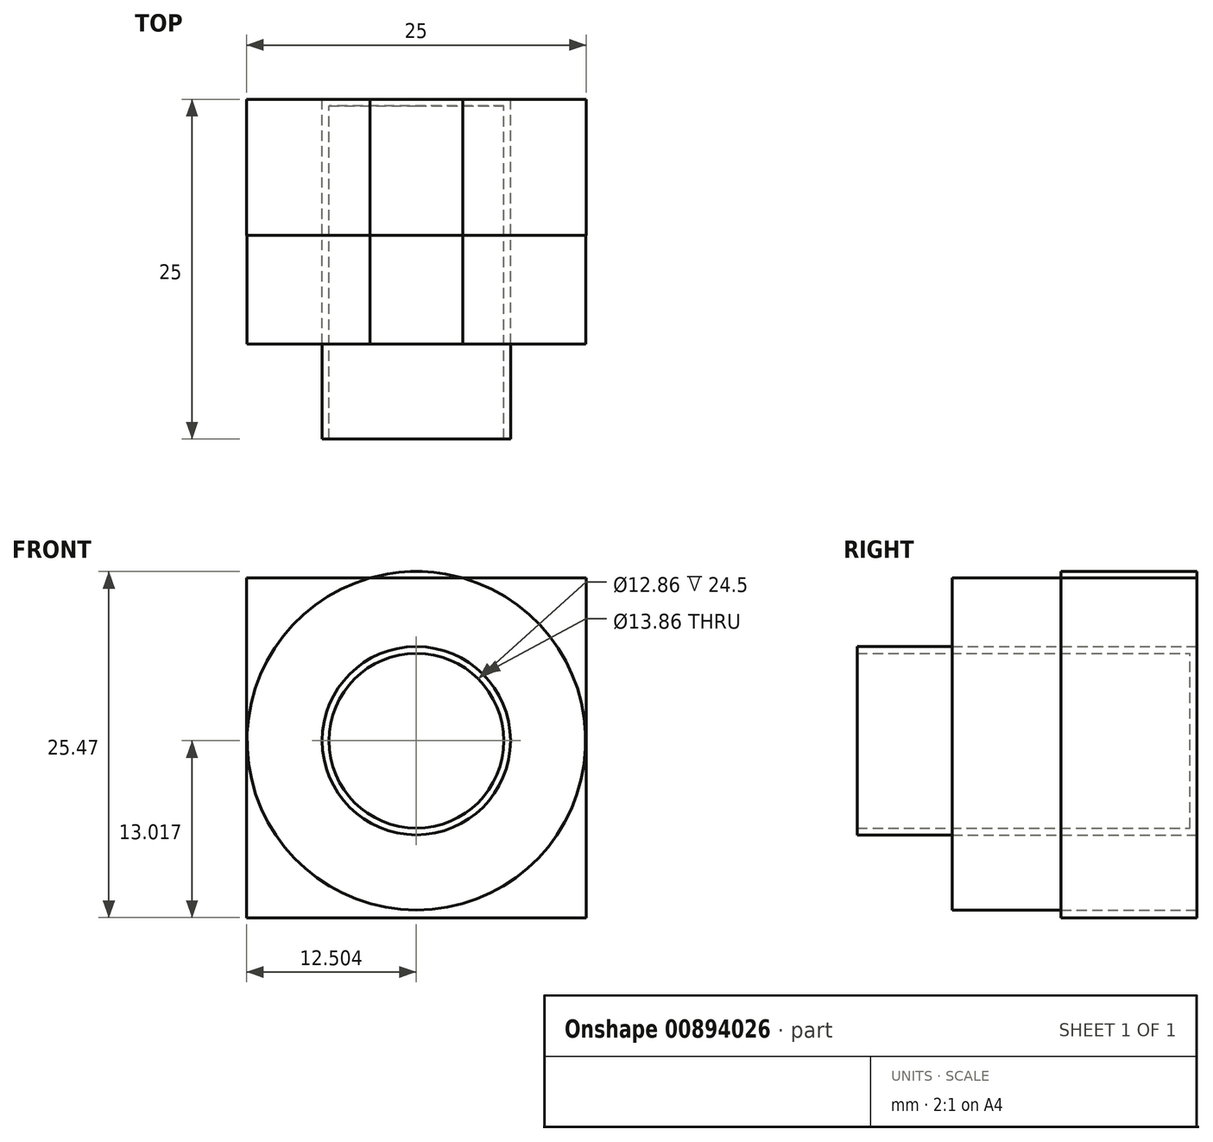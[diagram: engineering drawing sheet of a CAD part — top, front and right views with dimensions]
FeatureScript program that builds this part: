
annotation { "Feature Type Name" : "Feature", "Feature Type Description" : "" }
export const myFeature = defineFeature(function(context is Context, id is Id, definition is map)
    precondition{}
    {
        {
            var Q0;
            Q0=qCreatedBy(makeId("Front.planeOp"),FACE);
            var sketch = newSketch(context, id + "F0", { "sketchPlane" : qUnion([Q0])});
            skLineSegment(sketch, "E0.bottom", {"start": v(-12.07, -0.95) * mm, "end": v(-37.07, -0.95) * mm});
            skLineSegment(sketch, "E0.top", {"start": v(-12.07, 24.05) * mm, "end": v(-37.07, 24.05) * mm});
            skLineSegment(sketch, "E0.left", {"start": v(-12.07, -0.95) * mm, "end": v(-12.07, 24.05) * mm});
            skLineSegment(sketch, "E0.right", {"start": v(-37.07, -0.95) * mm, "end": v(-37.07, 24.05) * mm});
            skCircle(sketch, "E1", {"center": v(-24.57, 12.07) * mm, "radius": 12.45 * mm});
            skCircle(sketch, "E2", {"center": v(-24.57, 12.07) * mm, "radius": 6.93 * mm});
            skSolve(sketch);
        }
        {
            var Q0;
            Q0=makeQuery(id+"F0.imprint","IMPRINT",FACE,{"disambiguationData":[TD([[makeQuery(id+"F0.imprint","IMPRINT",EDGE,{"derivedFrom":sQuery(id+"F0.wireOp",EDGE,"E0.bottom")}),-1.0]])]});
            var Q1;
            {var subQ0=sQuery(id+"F0.wireOp",EDGE,"E1");var subQ1=sQuery(id+"F0.wireOp",EDGE,"E0.top");var subQ2=makeQuery(id+"F0.imprint","INTERSECT",VERTEX,{"disambiguationData":[OD(0.0)],"derivedFrom":[subQ1,subQ0]});Q1=makeQuery(id+"F0.imprint","IMPRINT",FACE,{"disambiguationData":[TD([[makeQuery(id+"F0.imprint","IMPRINT",EDGE,{"disambiguationData":[TD([[subQ2,-1.0]])],"derivedFrom":subQ1}),-1.0]])]});}
            extrude(context, id + "F1", {"entities" : qUnion([Q0, Q1]), "depth" : 10 * mm, "offsetDistance" : 25 * mm});
        }
        {
            var Q0;
            Q0=makeQuery(id+"F0.imprint","IMPRINT",FACE,{"disambiguationData":[TD([[makeQuery(id+"F0.imprint","IMPRINT",EDGE,{"derivedFrom":sQuery(id+"F0.wireOp",EDGE,"E2")}),1.0]])]});
            extrude(context, id + "F2", {"entities" : qUnion([Q0]), "depth" : 25 * mm, "offsetDistance" : 25 * mm});
        }
        {
            var Q0;
            Q0=makeQuery(id+"F0.imprint","IMPRINT",FACE,{"disambiguationData":[TD([[makeQuery(id+"F0.imprint","IMPRINT",EDGE,{"derivedFrom":sQuery(id+"F0.wireOp",EDGE,"E2")}),-1.0]])]});
            extrude(context, id + "F3", {"entities" : qUnion([Q0]), "depth" : 18 * mm, "offsetDistance" : 25 * mm});
        }
        {
            var Q0;
            Q0=makeQuery(id+"F2.opExtrude","CAP_FACE",FACE,{"disambiguationData":[OSD([sQuery(id+"F0.wireOp",EDGE,"E2")])],"isStart":false});
            shell(context, id + "F4", {"entities" : qUnion([Q0]), "thickness" : 0.5 * mm});
        }
    });
